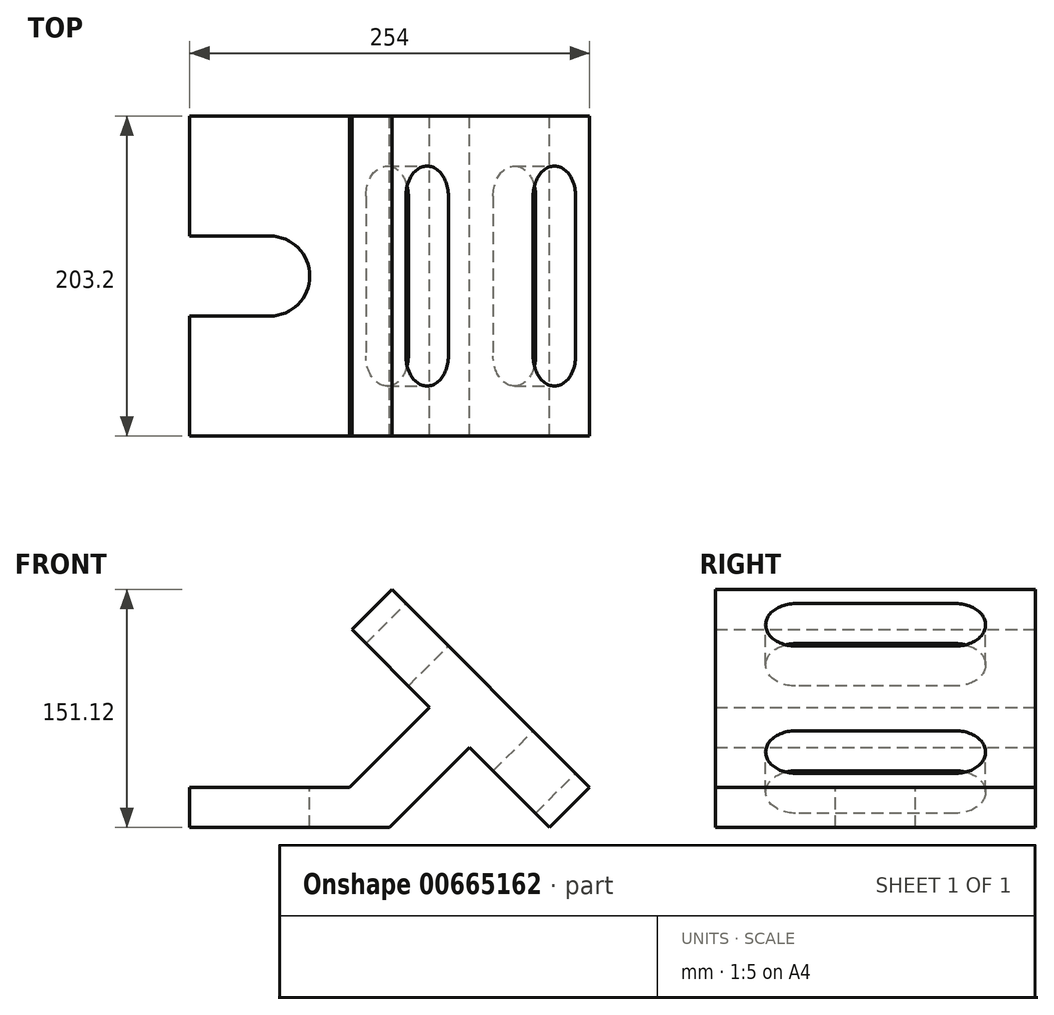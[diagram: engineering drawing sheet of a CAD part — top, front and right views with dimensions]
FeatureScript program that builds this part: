
annotation { "Feature Type Name" : "Feature", "Feature Type Description" : "" }
export const myFeature = defineFeature(function(context is Context, id is Id, definition is map)
    precondition{}
    {
        {
            var Q0;
            Q0=qCreatedBy(makeId("Front.planeOp"),FACE);
            var sketch = newSketch(context, id + "F0", { "sketchPlane" : qUnion([Q0])});
            skLineSegment(sketch, "E0", {"start": v(0, 0) * mm, "end": v(127, 0) * mm});
            skLineSegment(sketch, "E1", {"start": v(101.6, 25.4) * mm, "end": v(0, 25.4) * mm});
            skLineSegment(sketch, "E2", {"start": v(0, 25.4) * mm, "end": v(0, 0) * mm});
            skPoint(sketch, "E3", {"position": v(177.8, 50.8) * mm});
            skLineSegment(sketch, "E4", {"start": v(228.6, 0) * mm, "end": v(177.8, 50.8) * mm});
            skLineSegment(sketch, "E5", {"start": v(127, 0) * mm, "end": v(177.8, 50.8) * mm});
            skLineSegment(sketch, "E6", {"start": v(228.6, 0) * mm, "end": v(254, 25.4) * mm});
            skLineSegment(sketch, "E7.0", {"start": v(101.6, 25.4) * mm, "end": v(152.4, 76.2) * mm});
            skLineSegment(sketch, "E8", {"start": v(152.4, 76.2) * mm, "end": v(102.88, 125.72) * mm});
            skLineSegment(sketch, "E9", {"start": v(254, 25.4) * mm, "end": v(128.28, 151.12) * mm});
            skLineSegment(sketch, "E10", {"start": v(102.88, 125.72) * mm, "end": v(128.28, 151.12) * mm});
            skSolve(sketch);
        }
        {
            var Q0;
            Q0 = qSketchRegion(id + "F0", true);
            extrude(context, id + "F1", {"entities" : qUnion([Q0]), "endBound" : BoundingType.SYMMETRIC, "depth" : 203.2 * mm, "offsetDistance" : 25.4 * mm});
        }
        {
            var Q0;
            Q0=makeQuery(id+"F1.opExtrude","SWEPT_FACE",FACE,{"disambiguationData":[OSD([sQuery(id+"F0.wireOp",EDGE,"E9")])]});
            var sketch = newSketch(context, id + "F2", { "sketchPlane" : qUnion([Q0])});
            skLineSegment(sketch, "E11.0", {"start": v(-50.8, 3.46) * mm, "end": v(50.8, 3.46) * mm});
            skLineSegment(sketch, "E12.0", {"start": v(-50.8, -34.64) * mm, "end": v(50.8, -34.64) * mm});
            skLineSegment(sketch, "E13.0", {"start": v(-50.8, -148.94) * mm, "end": v(50.8, -148.94) * mm});
            skLineSegment(sketch, "E14.0", {"start": v(-50.8, -110.84) * mm, "end": v(50.8, -110.84) * mm});
            skArc(sketch, "E15", {"start": v(50.8, -34.64) * mm, "mid": v(69.85, -15.6) * mm, "end": v(50.8, 3.46) * mm});
            skArc(sketch, "E16", {"start": v(-50.8, 3.46) * mm, "mid": v(-69.85, -15.6) * mm, "end": v(-50.8, -34.64) * mm});
            skArc(sketch, "E17", {"start": v(-50.8, -110.84) * mm, "mid": v(-69.85, -129.9) * mm, "end": v(-50.8, -148.94) * mm});
            skArc(sketch, "E18", {"start": v(50.8, -148.94) * mm, "mid": v(69.85, -129.9) * mm, "end": v(50.8, -110.84) * mm});
            skSolve(sketch);
        }
        {
            var Q0;
            Q0=makeQuery(id+"F2.imprint","IMPRINT",FACE,{"disambiguationData":[TD([[makeQuery(id+"F2.imprint","IMPRINT",EDGE,{"derivedFrom":sQuery(id+"F2.wireOp",EDGE,"E11.0")}),-1.0]])]});
            var Q1;
            Q1=makeQuery(id+"F2.imprint","IMPRINT",FACE,{"disambiguationData":[TD([[makeQuery(id+"F2.imprint","IMPRINT",EDGE,{"derivedFrom":sQuery(id+"F2.wireOp",EDGE,"E13.0")}),1.0]])]});
            extrude(context, id + "F3", {"entities" : qUnion([Q0, Q1]), "operationType" : NewBodyOperationType.REMOVE, "oppositeDirection" : true, "depth" : 38.1 * mm, "offsetDistance" : 25.4 * mm});
        }
        {
            var Q0;
            Q0=makeQuery(id+"F1.opExtrude","SWEPT_FACE",FACE,{"disambiguationData":[OSD([sQuery(id+"F0.wireOp",EDGE,"E1")])]});
            var sketch = newSketch(context, id + "F4", { "sketchPlane" : qUnion([Q0])});
            skArc(sketch, "E19", {"start": v(50.8, -25.4) * mm, "mid": v(76.2, 0) * mm, "end": v(50.8, 25.4) * mm});
            skLineSegment(sketch, "E20", {"start": v(50.8, 25.4) * mm, "end": v(0, 25.4) * mm});
            skLineSegment(sketch, "E21", {"start": v(50.8, -25.4) * mm, "end": v(0, -25.4) * mm});
            skPoint(sketch, "E22.start.orphan", {"position": v(0, 0) * mm});
            skSolve(sketch);
        }
        {
            var Q0;
            Q0=makeQuery(id+"F4.imprint","IMPRINT",FACE,{"disambiguationData":[TD([[makeQuery(id+"F4.imprint","IMPRINT",EDGE,{"derivedFrom":sQuery(id+"F4.wireOp",EDGE,"E19")}),1.0]])]});
            extrude(context, id + "F5", {"entities" : qUnion([Q0]), "operationType" : NewBodyOperationType.REMOVE, "oppositeDirection" : true, "depth" : 25.4 * mm, "offsetDistance" : 25.4 * mm});
        }
    });
